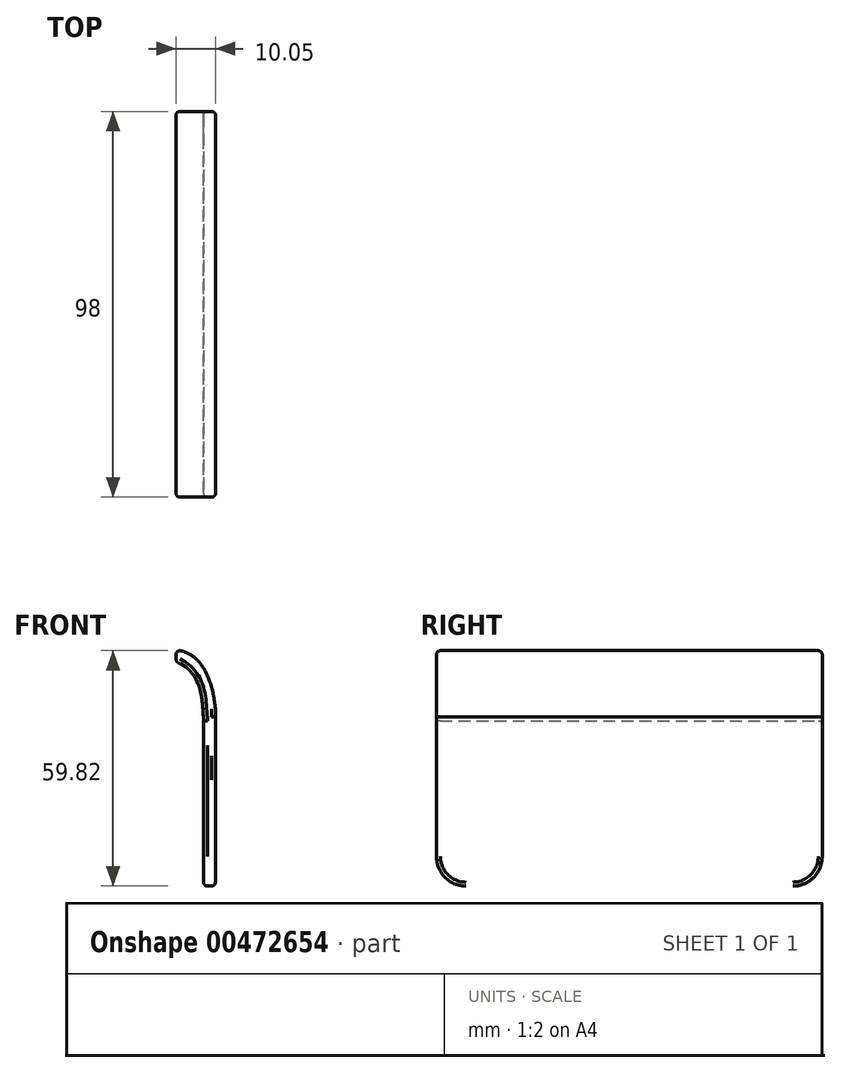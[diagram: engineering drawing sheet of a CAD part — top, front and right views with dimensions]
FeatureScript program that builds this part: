
annotation { "Feature Type Name" : "Feature", "Feature Type Description" : "" }
export const myFeature = defineFeature(function(context is Context, id is Id, definition is map)
    precondition{}
    {
        {
            var Q0;
            Q0=qCreatedBy(makeId("Front.planeOp"),FACE);
            var sketch = newSketch(context, id + "F0", { "sketchPlane" : qUnion([Q0])});
            skFitSpline(sketch, "E0", {"points": [v(-10, 60) * mm, v(0, 45.1) * mm, v(0, 42.98) * mm, v(0, 33.1) * mm, v(0, 26.92) * mm, v(0, 0) * mm], "startDerivative": vector(96.35, -9.35) * mm, "endDerivative": vector(0, -51.37) * mm});
            skLineSegment(sketch, "E1", {"start": v(-10, 60) * mm, "end": v(-10, 57) * mm});
            skLineSegment(sketch, "E2", {"start": v(0, 0) * mm, "end": v(-3, 0) * mm});
            skFitSpline(sketch, "E3", {"points": [v(-10, 57) * mm, v(-3.19, 45.2) * mm, v(-3, 42) * mm, v(-3.02, 33.3) * mm, v(-3.02, 26.37) * mm, v(-3, 0) * mm], "startDerivative": vector(81.95, -30.3) * mm, "endDerivative": vector(0, -98.94) * mm});
            skLineSegment(sketch, "E4", {"start": v(0, 26.92) * mm, "end": v(0, 45.1) * mm});
            skFitSpline(sketch, "E5.trimOffspring", {"points": [v(-10, 60) * mm, v(0, 45.1) * mm, v(0, 42.98) * mm, v(0, 33.1) * mm, v(0, 26.92) * mm, v(0, 0) * mm], "startDerivative": vector(96.35, -9.35) * mm, "endDerivative": vector(0, -51.37) * mm});
            skLineSegment(sketch, "E6", {"start": v(-3, 0) * mm, "end": v(-3, 78.92) * mm});
            skSolve(sketch);
        }
        {
            var Q0;
            Q0 = qSketchRegion(id + "F0", true);
            extrude(context, id + "F1", {"entities" : qUnion([Q0]), "depth" : 98 * mm});
        }
        {
            var Q0;
            Q0=makeQuery(id+"F1.opExtrude","CAP_EDGE",EDGE,{"disambiguationData":[OSD([sQuery(id+"F0.wireOp",EDGE,"E0")])],"isStart":false});
            var Q1;
            Q1=makeQuery(id+"F1.opExtrude","CAP_EDGE",EDGE,{"disambiguationData":[OSD([sQuery(id+"F0.wireOp",EDGE,"E3")])],"isStart":false});
            var Q2;
            Q2=makeQuery(id+"F1.opExtrude","SWEPT_EDGE",EDGE,{"disambiguationData":[OSD([sQuery(id+"F0.wireOp",EDGE,"E2"),sQuery(id+"F0.wireOp",EDGE,"E5.trimOffspring")])]});
            var Q3;
            Q3=makeQuery(id+"F1.opExtrude","SWEPT_EDGE",EDGE,{"disambiguationData":[OSD([sQuery(id+"F0.wireOp",EDGE,"E2"),sQuery(id+"F0.wireOp",EDGE,"E3")])]});
            var Q4;
            Q4=makeQuery(id+"F1.opExtrude","CAP_EDGE",EDGE,{"disambiguationData":[OSD([sQuery(id+"F0.wireOp",EDGE,"E5.trimOffspring")])],"isStart":true});
            var Q5;
            Q5=makeQuery(id+"F1.opExtrude","CAP_EDGE",EDGE,{"disambiguationData":[OSD([sQuery(id+"F0.wireOp",EDGE,"E0")])],"isStart":true});
            var Q6;
            Q6=makeQuery(id+"F1.opExtrude","CAP_EDGE",EDGE,{"disambiguationData":[OSD([sQuery(id+"F0.wireOp",EDGE,"E3")])],"isStart":true});
            var Q7;
            Q7=makeQuery(id+"F1.opExtrude","SWEPT_EDGE",EDGE,{"disambiguationData":[OSD([sQuery(id+"F0.wireOp",EDGE,"E1"),sQuery(id+"F0.wireOp",EDGE,"E3")])]});
            var Q8;
            Q8=makeQuery(id+"F1.opExtrude","SWEPT_EDGE",EDGE,{"disambiguationData":[OSD([sQuery(id+"F0.wireOp",EDGE,"E0"),sQuery(id+"F0.wireOp",EDGE,"E1")])]});
            var Q9;
            Q9=makeQuery(id+"F1.opExtrude","CAP_EDGE",EDGE,{"disambiguationData":[OSD([sQuery(id+"F0.wireOp",EDGE,"E1")])],"isStart":false});
            var Q10;
            Q10=makeQuery(id+"F1.opExtrude","CAP_EDGE",EDGE,{"disambiguationData":[OSD([sQuery(id+"F0.wireOp",EDGE,"E1")])],"isStart":true});
            fillet(context, id + "F2", {"entities" : qUnion([Q0, Q1, Q2, Q3, Q4, Q5, Q6, Q7, Q8, Q9, Q10]), "radius" : 1 * mm, "tangentPropagation" : true, "allowEdgeOverflow" : false});
        }
        {
            var Q0;
            Q0=makeQuery(id+"F1.opExtrude","CAP_EDGE",EDGE,{"disambiguationData":[OSD([sQuery(id+"F0.wireOp",EDGE,"E2")])],"isStart":false});
            var Q1;
            Q1=makeQuery(id+"F1.opExtrude","CAP_EDGE",EDGE,{"disambiguationData":[OSD([sQuery(id+"F0.wireOp",EDGE,"E2")])],"isStart":true});
            fillet(context, id + "F3", {"entities" : qUnion([Q0, Q1]), "radius" : 7.5 * mm, "tangentPropagation" : true, "allowEdgeOverflow" : false});
        }
    });
